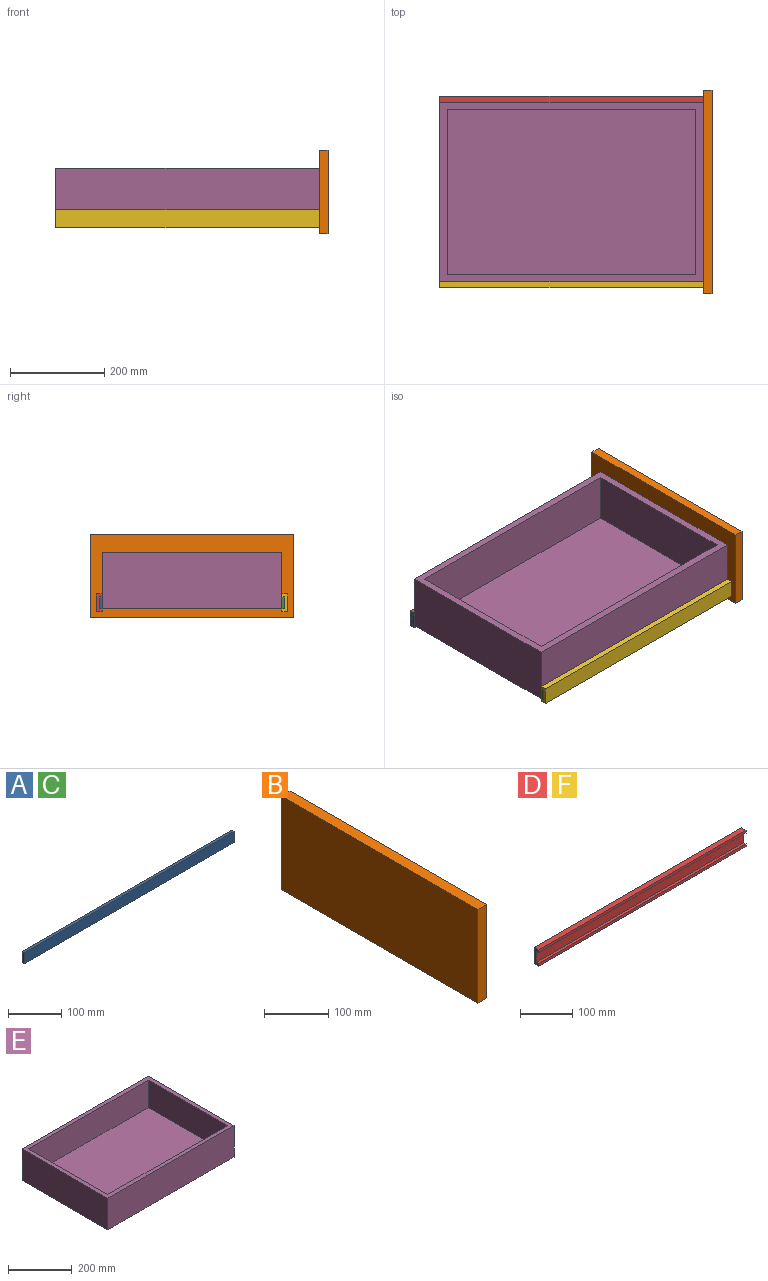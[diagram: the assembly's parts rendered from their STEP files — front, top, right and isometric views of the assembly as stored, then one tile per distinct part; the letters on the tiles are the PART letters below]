
ASSEMBLY  parts=6 mates=6
PART A: 6 faces, bbox 558.8x6.4x25.4 mm
  f0: plane 25.4x6.35mm, normal (1,0,0), area 161.3mm2, adj f1,f2,f3,f4
  f1: plane 558.8x6.35mm, normal (0,0,1), area 3548.4mm2, adj f0,f2,f4,f5
  f2: plane 558.8x25.4mm, normal (0,-1,0), area 14193.5mm2, adj f0,f1,f3,f5
  f3: plane 558.8x6.35mm, normal (0,0,-1), area 3548.4mm2, adj f0,f2,f4,f5
  f4: plane 558.8x25.4mm, normal (0,1,0), area 14193.5mm2, adj f0,f1,f3,f5
  f5: plane 25.4x6.35mm, normal (-1,0,0), area 161.3mm2, adj f1,f2,f3,f4
PART B: 11 faces, bbox 19.1x431.8x177.8 mm
  f0: plane 177.8x19.05mm, normal (0,1,0), area 3387.1mm2, adj f1,f7,f8,f9
  f1: plane 431.8x19.05mm, normal (0,0,1), area 8225.8mm2, adj f0,f2,f8,f9
  f2: plane 177.8x19.05mm, normal (0,-1,0), area 3387.1mm2, adj f1,f7,f8,f9
  f3: plane 101.6x6.35mm, normal (0,1,0), area 645.2mm2, adj f4,f6,f8,f10
  f4: plane 355.6x6.35mm, normal (0,0,-1), area 2258.1mm2, adj f3,f5,f8,f10
  f5: plane 101.6x6.35mm, normal (0,-1,0), area 645.2mm2, adj f4,f6,f8,f10
  f6: plane 355.6x6.35mm, normal (0,0,1), area 2258.1mm2, adj f3,f5,f8,f10
  f7: plane 431.8x19.05mm, normal (0,0,-1), area 8225.8mm2, adj f0,f2,f8,f9
  f8: plane 431.8x177.8mm, normal (1,0,0), area 40645.1mm2, adj f0,f1,f2,f3,f4,f5,f6,f7
  f9: plane 431.8x177.8mm, normal (-1,0,0), area 76774mm2, adj f0,f1,f2,f7
  f10: plane 355.6x101.6mm, normal (1,0,0), area 36129mm2, adj f3,f4,f5,f6
PART C: same geometry as A
PART D: 10 faces, bbox 558.8x12.7x38.1 mm
  f0: plane 38.1x12.7mm, normal (1,0,0), area 322.6mm2, adj f1,f2,f3,f4,f5,f7,f8,f9
  f1: plane 558.8x12.7mm, normal (0,0,-1), area 7096.8mm2, adj f0,f2,f6,f8
  f2: plane 558.8x38.1mm, normal (0,1,0), area 21290.3mm2, adj f0,f1,f3,f6
  f3: plane 558.8x12.7mm, normal (0,0,1), area 7096.8mm2, adj f0,f2,f4,f6
  f4: plane 558.8x6.35mm, normal (0,-1,0), area 3548.4mm2, adj f0,f3,f5,f6
  f5: plane 558.8x6.35mm, normal (0,0,-1), area 3548.4mm2, adj f0,f4,f6,f7
  f6: plane 38.1x12.7mm, normal (-1,0,0), area 322.6mm2, adj f1,f2,f3,f4,f5,f7,f8,f9
  f7: plane 558.8x25.4mm, normal (0,-1,0), area 14193.5mm2, adj f0,f5,f6,f9
  f8: plane 558.8x6.35mm, normal (0,-1,0), area 3548.4mm2, adj f0,f1,f6,f9
  f9: plane 558.8x6.35mm, normal (0,0,1), area 3548.4mm2, adj f0,f6,f7,f8
PART E: 11 faces, bbox 558.8x381x120.7 mm
  f0: plane 558.8x381mm, normal (0,0,1), area 27716.1mm2, adj f1,f2,f4,f5,f6,f7,f9,f10
  f1: plane 558.8x120.65mm, normal (0,1,0), area 67419.2mm2, adj f0,f3,f4,f5
  f2: plane 558.8x120.65mm, normal (0,-1,0), area 67419.2mm2, adj f0,f3,f4,f5
  f3: plane 558.8x381mm, normal (0,0,-1), area 212902.8mm2, adj f1,f2,f4,f5
  f4: plane 381x120.65mm, normal (1,0,0), area 45967.6mm2, adj f0,f1,f2,f3
  f5: plane 381x120.65mm, normal (-1,0,0), area 45967.6mm2, adj f0,f1,f2,f3
  f6: plane 528.32x105.41mm, normal (0,-1,0), area 55690.2mm2, adj f0,f8,f9,f10
  f7: plane 528.32x105.41mm, normal (0,1,0), area 55690.2mm2, adj f0,f8,f9,f10
  f8: plane 528.32x350.52mm, normal (0,0,1), area 185186.7mm2, adj f6,f7,f9,f10
  f9: plane 350.52x105.41mm, normal (-1,0,0), area 36948.3mm2, adj f0,f6,f7,f8
  f10: plane 350.52x105.41mm, normal (1,0,0), area 36948.3mm2, adj f0,f6,f7,f8
PART F: same geometry as D
PLACE A t=(-668.55,-83.57,16.38)mm
PLACE B t=(-668.55,-83.57,16.38)mm
PLACE C rot(axis=(0,0,1),180deg) t=(-109.75,399.03,16.38)mm
PLACE D t=(-668.55,-83.57,16.38)mm fixed
PLACE E t=(-668.55,-83.57,16.38)mm
PLACE F rot(axis=(0,0,1),180deg) t=(-109.75,399.03,16.38)mm
MATE fastened B.f9 <-> E.f4  axis (-1,0,0) through (-109.75,157.73,41.78)mm
MATE planar F.f7 <-> C.f4  axis (0,1,0) through (-668.55,-39.12,73.53)mm
MATE planar A.f4 <-> D.f7  axis (0,1,0) through (-668.55,354.58,73.53)mm
MATE fastened A.f5 <-> E.f5  axis (-1,0,0) through (-668.55,348.23,60.83)mm
MATE planar D.f6 <-> F.f0  axis (-1,0,0) through (-668.55,356.16,73.53)mm
MATE fastened E.f5 <-> C.f0  axis (-1,0,0) through (-668.55,-32.77,60.83)mm
